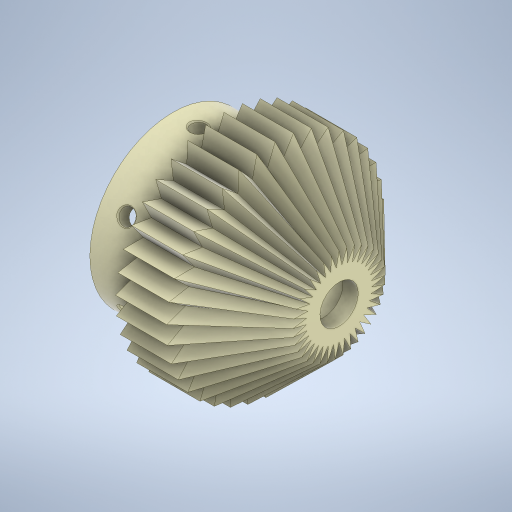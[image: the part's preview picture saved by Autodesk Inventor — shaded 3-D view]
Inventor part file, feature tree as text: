
AUTODESK INVENTOR PART (.ipt)
format: ipt  version: 2023 (Build 270158030, 158C)  size: 653,312 bytes
history: native  units: in
note: dims shown in document units (in); Inventor stores cm internally (conversion verified against a paired STEP export)
features: sketch x8, extrude x4, pattern_circular x3, other x2, loft x1, revolve x1, plane x1, hole x1
ambient origin geometry x8: Origin, YZ Plane, XZ Plane, XY Plane, X Axis, Y Axis, Z Axis, Center Point
bodies: Solid1 (feature_tree)
feature tree (21):
  other  "Main Body"
  extrude  "Teeth"  TaperAngle=45.0deg  [1 undecoded]
  pattern_circular  "Circular Pattern1"  Count=2  [1 undecoded]
  loft  "Angle Teeth"
  pattern_circular  "Circular Pattern2"  Count=37 Angle=360.0deg
  extrude  "Extrusion4"  Depth=0.3937in
  revolve  "Revolution2"  [1 undecoded]
  extrude  "Extrusion5"  Depth=0.3937in
  extrude  "Extrusion6"  Depth=0.3937in
  plane  "Work Plane1"
  hole  "Hole1"  [1 undecoded]
  pattern_circular  "Circular Pattern3"  Angle=90.0deg  [1 undecoded]
  sketch  "Sketch1"  dims[d0=0.7874in d1=45.0deg]
  sketch  "Sketch6"  dims[d2=0.5906in]
  sketch  "Sketch11"  dims[d3=2.5591in]
  other  "Edges2"
  sketch  "Sketch12"  dims[d4=90.0deg]
  sketch  "Sketch14"  dims[d18=45.0deg]
  sketch  "Sketch15"  dims[d19=0.3937in d20=0.7874in d21=0.0in]
  sketch  "Sketch16"  dims[d22=14.5669in d23=360.0deg d25=0.0in d26=90.0deg]
  sketch  "Sketch18"  dims[d27=0.0in d28=90.0deg d29=14.5669in d30=360.0deg d32=0.5906in d33=0.0in d34=0.0in d35=0.7874in d36=1.2205in d37=0.3937in d38=90.0deg d39=1.0236in d40=1.5354in d41=0.0in d42=0.7874in d43=0.0in d45=2.1654in d46=0.1969in d47=0.2362in d48=0.3389in d49=0.2756in d50=0.0787in d51=90.0deg d52=0.6167in d53=0.8108in d54=0.3937in d55=2.3622in d56=360.0deg]
note: 5 required parameter values undecoded (feature->parameter linkage not recoverable at this tier; creation-order binding heuristic only, values carry confidence <= 0.55)